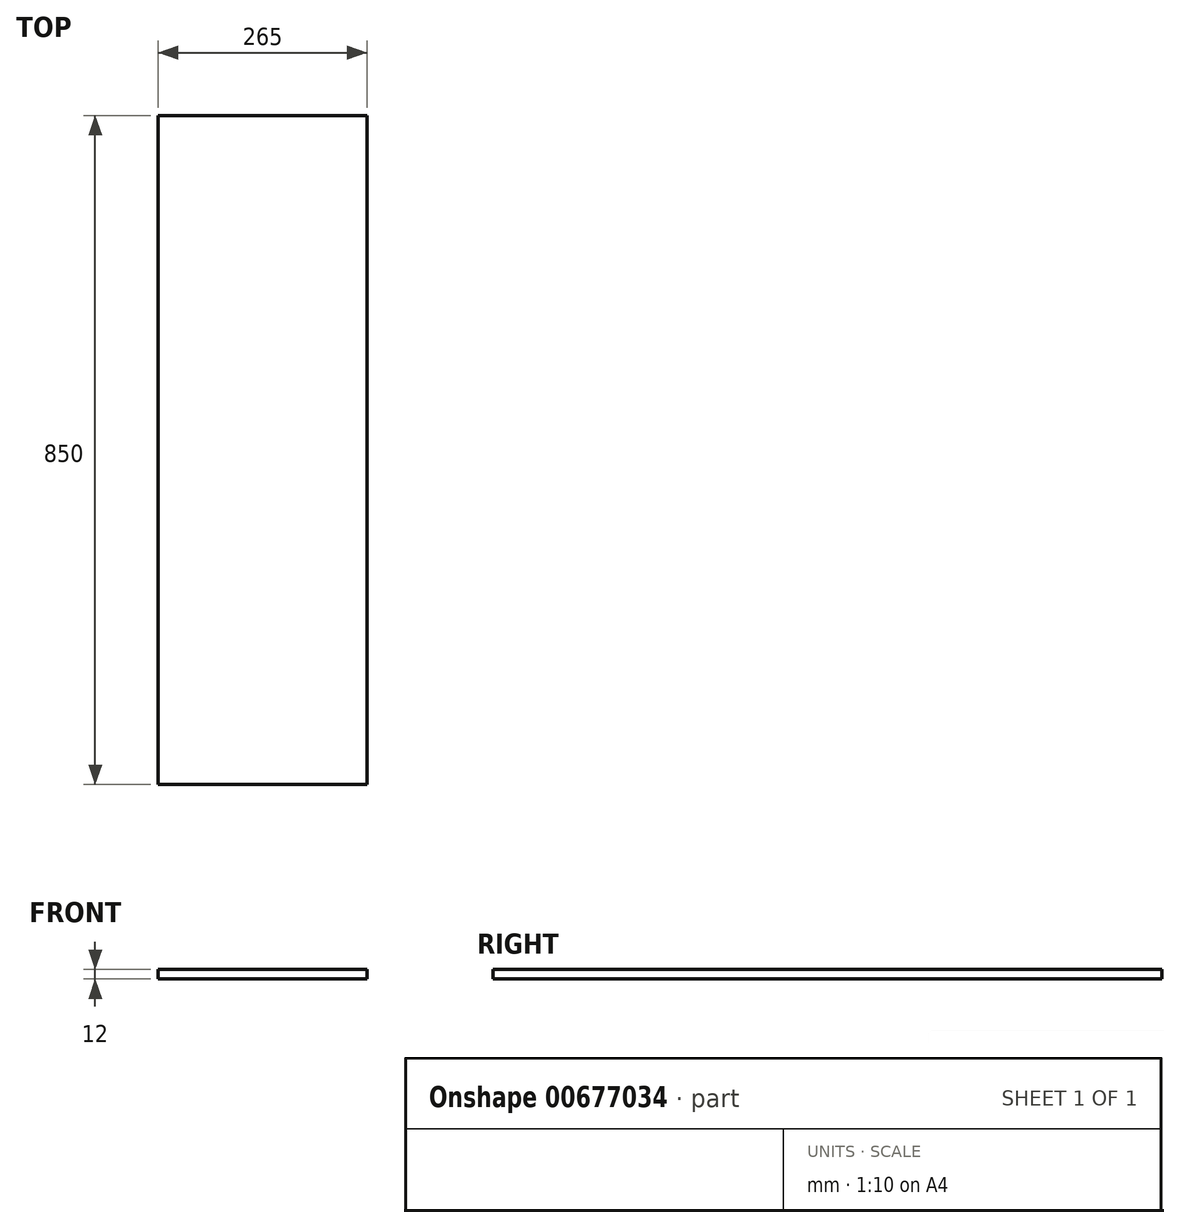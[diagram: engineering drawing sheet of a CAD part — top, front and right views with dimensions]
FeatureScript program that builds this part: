
annotation { "Feature Type Name" : "Feature", "Feature Type Description" : "" }
export const myFeature = defineFeature(function(context is Context, id is Id, definition is map)
    precondition{}
    {
        {
            var Q0;
            Q0=qCreatedBy(makeId("Top.planeOp"),FACE);
            var sketch = newSketch(context, id + "F0", { "sketchPlane" : qUnion([Q0])});
            skLineSegment(sketch, "E0.bottom", {"start": v(-125, 425) * mm, "end": v(140, 425) * mm});
            skLineSegment(sketch, "E0.top", {"start": v(-125, -425) * mm, "end": v(140, -425) * mm});
            skLineSegment(sketch, "E0.left", {"start": v(-125, 425) * mm, "end": v(-125, -425) * mm});
            skLineSegment(sketch, "E0.right", {"start": v(140, 425) * mm, "end": v(140, -425) * mm});
            skSolve(sketch);
        }
        {
            var Q0;
            Q0=makeQuery(id+"F0.imprint","IMPRINT",FACE,{"disambiguationData":[TD([[makeQuery(id+"F0.imprint","IMPRINT",EDGE,{"derivedFrom":sQuery(id+"F0.wireOp",EDGE,"E0.bottom")}),-1.0]])]});
            var Q1;
            Q1 = qConstructionFilter(qBodyType(qCreatedBy(id + "F0" ,EDGE), BodyType.WIRE), ConstructionObject.NO);
            extrude(context, id + "F1", {"entities" : qUnion([Q0]), "surfaceEntities" : qUnion([Q1]), "depth" : 12 * mm, "offsetDistance" : 25 * mm});
        }
    });
